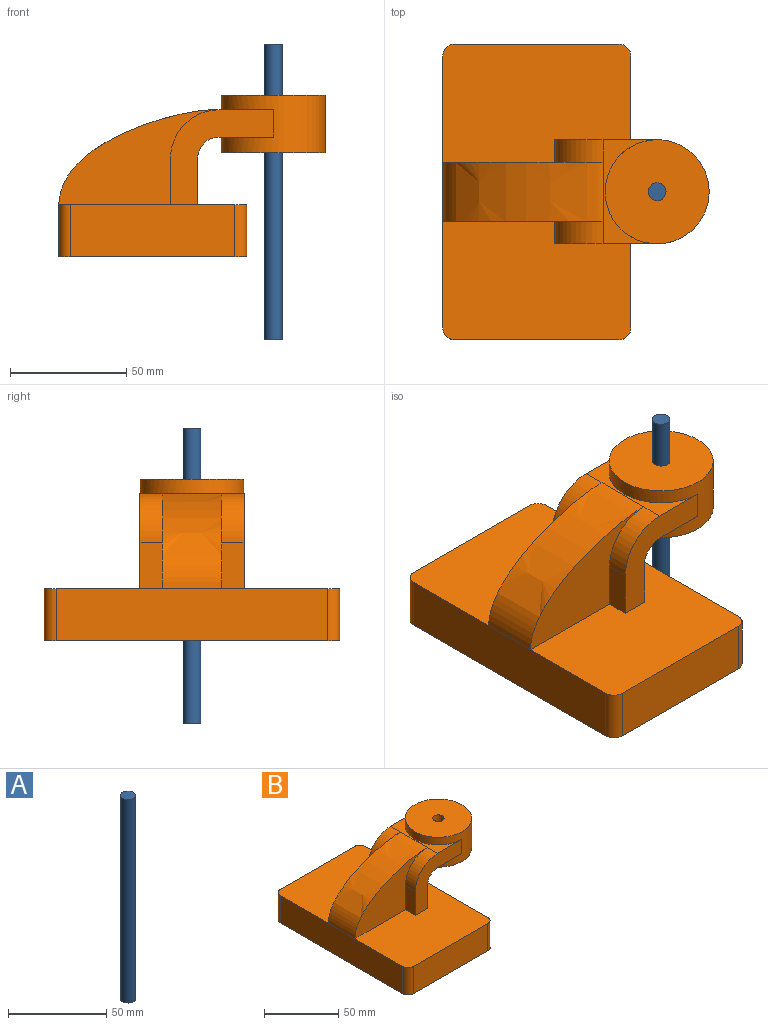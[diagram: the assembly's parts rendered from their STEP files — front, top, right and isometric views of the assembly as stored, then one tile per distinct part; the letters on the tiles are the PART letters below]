
ASSEMBLY  parts=2 mates=1
PART A: 3 faces, bbox 7.6x7.6x127 mm
  f0: cylinder r=3.81mm len=127mm, axis (0,0,-1), area 3040.2mm2, adj f1,f2
  f1: plane 7.62x7.62mm, normal (0,0,1), area 45.6mm2, adj f0
  f2: plane 7.62x7.62mm, normal (0,0,-1), area 45.6mm2, adj f0
PART B: 30 faces, bbox 114.5x127x69.5 mm
  f0: plane 127x80.8mm, normal (0,0,1), area 8496.7mm2, adj f2,f3,f5,f6,f7,f11,f12,f14
  f1: cylinder r=20.87mm len=20.87mm, axis (0,1,0), area 316.4mm2, adj f2,f9,f15,f18
  f2: plane 19.88x9.65mm, normal (-1,0,0), area 191.9mm2, adj f0,f1,f15,f18
  f3: plane 116.84x22.47mm, normal (-1,0,0), area 2624.8mm2, adj f0,f4,f16,f19,f21
  f4: plane 127x80.8mm, normal (0,0,-1), area 10239.2mm2, adj f3,f5,f6,f7,f19,f20,f21,f22
  f5: plane 116.84x22.47mm, normal (1,0,0), area 2624.8mm2, adj f0,f4,f20,f22
  f6: plane 70.64x22.47mm, normal (0,-1,0), area 1586.9mm2, adj f0,f4,f21,f22
  f7: plane 70.64x22.47mm, normal (0,1,0), area 1586.9mm2, adj f0,f4,f19,f20
  f8: plane 44.7x23.24mm, normal (0,0,-1), area 254mm2, adj f13,f14,f15,f24
  f9: plane 44.7x23.24mm, normal (0,0,1), area 254mm2, adj f1,f10,f14,f15,f16,f24
  f10: cylinder r=20.87mm len=20.87mm, axis (0,1,0), area 316.4mm2, adj f9,f11,f14,f17
  f11: plane 19.88x9.65mm, normal (-1,0,0), area 191.9mm2, adj f0,f10,f14,f17
  f12: plane 44.7x19.88mm, normal (1,0,0), area 888.6mm2, adj f0,f13,f14,f15
  f13: cylinder r=9.19mm len=44.7mm, axis (0,1,0), area 645.1mm2, adj f8,f12,f14,f15
  f14: plane 44.11x40.75mm, normal (0,-1,0), area 779.6mm2, adj f0,f8,f9,f10,f11,f12,f13,f24
  f15: plane 44.11x40.75mm, normal (0,1,0), area 779.6mm2, adj f0,f1,f2,f8,f9,f12,f13,f24
  f16: extruded ~68.91x40.86mm, area 2191.2mm2, adj f3,f9,f17,f18
  f17: plane 68.91x42.27mm, normal (0,-1,0), area 1362.5mm2, adj f0,f10,f11,f16
  f18: plane 68.91x42.27mm, normal (0,1,0), area 1362.5mm2, adj f0,f1,f2,f16
  f19: cylinder r=5.08mm len=22.47mm, axis (0,0,-1), area 179.3mm2, adj f0,f3,f4,f7
  f20: cylinder r=5.08mm len=22.47mm, axis (0,0,1), area 179.3mm2, adj f0,f4,f5,f7
  f21: cylinder r=5.08mm len=22.47mm, axis (0,0,1), area 179.3mm2, adj f0,f3,f4,f6
  f22: cylinder r=5.08mm len=22.47mm, axis (0,0,-1), area 179.3mm2, adj f0,f4,f5,f6
  f23: cylinder r=3.81mm len=24.59mm, axis (0,0,1), area 448.8mm2, adj f25,f26,f27,f28,f29
  f24: cylinder r=22.35mm len=44.7mm, axis (0,0,1), area 2632.9mm2, adj f8,f9,f14,f15,f25,f26
  f25: plane 44.7x44.7mm, normal (0,0,1), area 1524mm2, adj f23,f24
  f26: plane 44.7x44.7mm, normal (0,0,-1), area 1524mm2, adj f23,f24
  f27: plane 7.62x3.81mm, normal (0,0,1), area 22.8mm2, adj f23,f28
  f28: plane 11.68x7.62mm, normal (1,0,0), area 89mm2, adj f23,f27,f29
  f29: plane 7.62x3.81mm, normal (0,0,-1), area 22.8mm2, adj f23,f28
PLACE A t=(98.99,70.57,-146.42)mm
PLACE B rot(axis=(0,0,-1),0deg) t=(47.24,70.57,-163.08)mm
MATE slider B.f23 <-> A.f0  axis (0,0,-1) through (98.99,70.57,-129.45)mm
